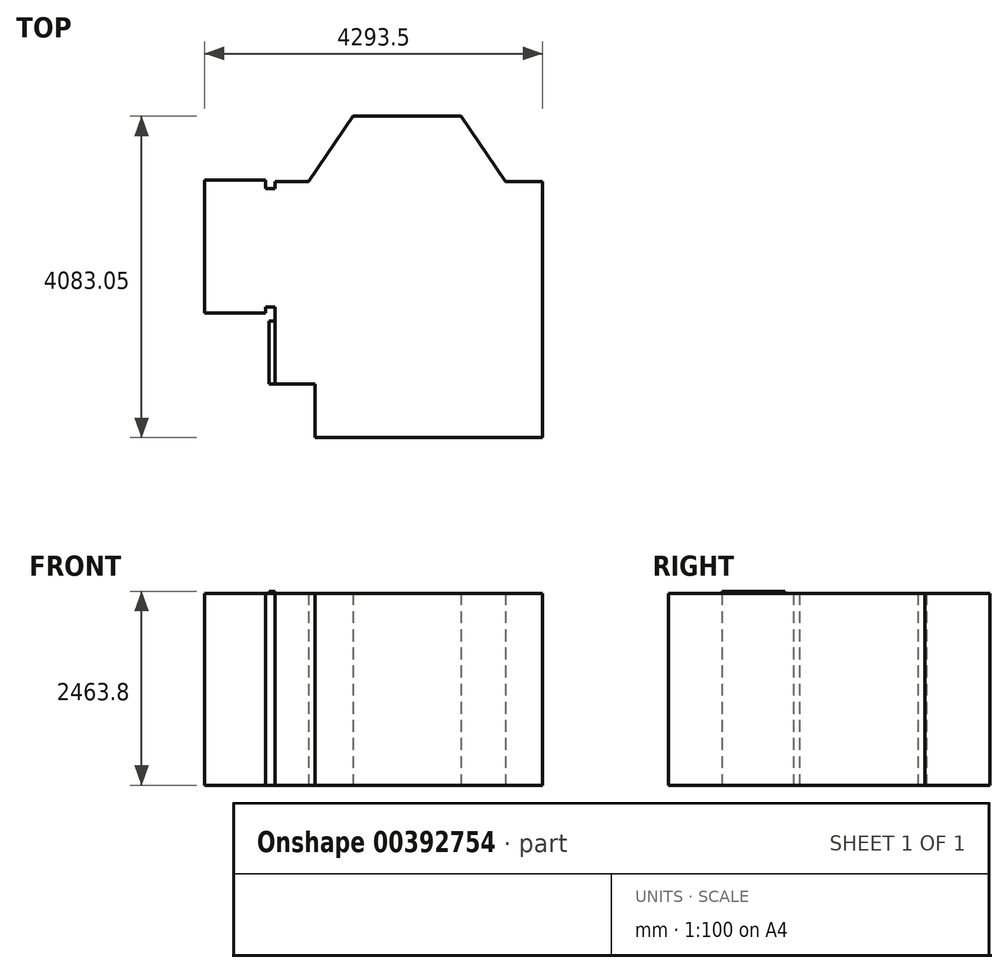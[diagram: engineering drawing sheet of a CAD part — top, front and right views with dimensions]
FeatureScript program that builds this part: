
annotation { "Feature Type Name" : "Feature", "Feature Type Description" : "" }
export const myFeature = defineFeature(function(context is Context, id is Id, definition is map)
    precondition{}
    {
        {
            var Q0;
            Q0=qCreatedBy(makeId("Top.planeOp"),FACE);
            var sketch = newSketch(context, id + "F0", { "sketchPlane" : qUnion([Q0])});
            skLineSegment(sketch, "E0", {"start": v(486.23, 4083.05) * mm, "end": v(1857.83, 4083.05) * mm});
            skLineSegment(sketch, "E1", {"start": v(2423.43, 3254.38) * mm, "end": v(2893.33, 3254.38) * mm});
            skLineSegment(sketch, "E2", {"start": v(2893.33, 3254.38) * mm, "end": v(2893.33, 0) * mm});
            skLineSegment(sketch, "E3", {"start": v(2893.33, 0) * mm, "end": v(0, 0) * mm});
            skLineSegment(sketch, "E4", {"start": v(0, 0) * mm, "end": v(0, 679.45) * mm});
            skLineSegment(sketch, "E5", {"start": v(0, 679.45) * mm, "end": v(-508, 679.45) * mm});
            skLineSegment(sketch, "E6", {"start": v(-1400.18, 3273.43) * mm, "end": v(-625.48, 3273.43) * mm});
            skLineSegment(sketch, "E7", {"start": v(-625.48, 3273.43) * mm, "end": v(-625.48, 3165.48) * mm});
            skLineSegment(sketch, "E8", {"start": v(-625.48, 3165.47) * mm, "end": v(-508, 3165.47) * mm});
            skLineSegment(sketch, "E9", {"start": v(-508, 3165.48) * mm, "end": v(-508, 3254.38) * mm});
            skLineSegment(sketch, "E10", {"start": v(-508, 3254.38) * mm, "end": v(-79.38, 3254.38) * mm});
            skLineSegment(sketch, "E11", {"start": v(-508, 1479.55) * mm, "end": v(-508, 679.45) * mm});
            skLineSegment(sketch, "E12", {"start": v(1857.83, 4083.05) * mm, "end": v(2423.43, 3254.38) * mm});
            skLineSegment(sketch, "E13", {"start": v(486.23, 4083.05) * mm, "end": v(-79.38, 3254.38) * mm});
            skLineSegment(sketch, "E14", {"start": v(-1400.18, 3273.43) * mm, "end": v(-1400.18, 1584.33) * mm});
            skLineSegment(sketch, "E15", {"start": v(-1400.18, 1584.33) * mm, "end": v(-628.65, 1584.33) * mm});
            skLineSegment(sketch, "E16", {"start": v(-628.65, 1584.33) * mm, "end": v(-628.65, 1660.53) * mm});
            skLineSegment(sketch, "E17", {"start": v(-628.65, 1660.53) * mm, "end": v(-508, 1660.53) * mm});
            skLineSegment(sketch, "E18", {"start": v(-508, 1660.53) * mm, "end": v(-508, 1479.55) * mm});
            skSolve(sketch);
        }
        {
            var Q0;
            Q0=makeQuery(id+"F0.imprint","IMPRINT",FACE,{"disambiguationData":[TD([[makeQuery(id+"F0.imprint","IMPRINT",EDGE,{"derivedFrom":sQuery(id+"F0.wireOp",EDGE,"E0")}),-1.0]])]});
            extrude(context, id + "F1", {"entities" : qUnion([Q0]), "depth" : 2438.4 * mm});
        }
        {
            var Q0;
            Q0=makeQuery(id+"F1.opExtrude","CAP_FACE",FACE,{"disambiguationData":[OSD([sQuery(id+"F0.wireOp",EDGE,"E0"),sQuery(id+"F0.wireOp",EDGE,"jz9IxRy3-2qm7-KJ3F-O2Oc-06IpkQuKulIh"),sQuery(id+"F0.wireOp",EDGE,"E1"),sQuery(id+"F0.wireOp",EDGE,"E2"),sQuery(id+"F0.wireOp",EDGE,"E3"),sQuery(id+"F0.wireOp",EDGE,"E4"),sQuery(id+"F0.wireOp",EDGE,"E5"),sQuery(id+"F0.wireOp",EDGE,"FUplDghn-5Lox-xBSY-5qyk-6HsgQjmysgEg"),sQuery(id+"F0.wireOp",EDGE,"gvitSr2r-Pvfc-yV1F-nBRl-78NfxfF57529"),sQuery(id+"F0.wireOp",EDGE,"XyL6uuFk-02hg-V4uP-gYeK-Q0rYduNwpJKh"),sQuery(id+"F0.wireOp",EDGE,"WSV7V8oe-dxlr-9pHG-y24E-ps1iRwDZXgyD"),sQuery(id+"F0.wireOp",EDGE,"E6"),sQuery(id+"F0.wireOp",EDGE,"E7"),sQuery(id+"F0.wireOp",EDGE,"E8"),sQuery(id+"F0.wireOp",EDGE,"3qHi5SbZ-BnVn-JmwR-pvkG-6sx2vJhihQJN"),sQuery(id+"F0.wireOp",EDGE,"NkcAHPtc-cwMC-poy6-ij30-RYtlhWaET2uh"),sQuery(id+"F0.wireOp",EDGE,"E9"),sQuery(id+"F0.wireOp",EDGE,"E10"),sQuery(id+"F0.wireOp",EDGE,"E11")])],"isStart":false});
            var sketch = newSketch(context, id + "F2", { "sketchPlane" : qUnion([Q0])});
            skLineSegment(sketch, "E19.0", {"start": v(0, 679.45) * mm, "end": v(-508, 679.45) * mm});
            skLineSegment(sketch, "E20.bottom", {"start": v(-508, 679.45) * mm, "end": v(-584.2, 679.45) * mm});
            skLineSegment(sketch, "E20.top", {"start": v(-508, 1479.55) * mm, "end": v(-584.2, 1479.55) * mm});
            skLineSegment(sketch, "E20.left", {"start": v(-508, 679.45) * mm, "end": v(-508, 1479.55) * mm});
            skLineSegment(sketch, "E20.right", {"start": v(-584.2, 679.45) * mm, "end": v(-584.2, 1479.55) * mm});
            skSolve(sketch);
        }
        {
            var Q0;
            Q0=makeQuery(id+"F2.imprint","IMPRINT",FACE,{"disambiguationData":[TD([[makeQuery(id+"F2.imprint","IMPRINT",EDGE,{"derivedFrom":sQuery(id+"F2.wireOp",EDGE,"E20.bottom")}),-1.0]])]});
            extrude(context, id + "F3", {"entities" : qUnion([Q0]), "operationType" : NewBodyOperationType.ADD, "depth" : 25.4 * mm});
        }
    });
